# Revit family: PURY-EM200YNW-A
name_source: partatom
category: Mechanical Equipment
revit_build: Autodesk Revit 2016 (Build: 20150220_1215(x64)
units: mm (PartAtom-declared; Revit-internal decimal feet)

## family parameters
Always vertical = Yes
Cut with Voids When Loaded = No
OmniClass Number = 23.75.00.00
OmniClass Title = Climate Control (HVAC)
Part Type = Normal
Room Calculation Point = No
Round Connector Dimension = Use Radius
Shared = No
Work Plane-Based = No

## types (6) — shared parameters
Airflow Rate (m3/h) = 10200
Airflow Rate (m3/min) = 170
Compressor Motor Output (kW) = 6
Compressor_Lubricant = MEL46EH
Compressor_Quantity = 1
Compressor_Type = Inverter scroll hermetic compressor
Cooling Capacity (kW) = 22.4
Cooling EER (kW/kW) = 3.64
Cooling Power Input (kW) = 6.15
Depth = 740 mm  [stored 2.42782 ft]
External Finish = Pre-coated galvanized steel sheets (+powder coating for -BS type) <MUNSELL 5Y 8/1 or similar>
Fan Motor Output (kW) = 0.92
Fan_Quantity = 1
Fan_Type = Propeller Fan
Heating COP (kW/kW) = 3.69
Heating Capacity (kW) = 25
Heating Power Input (kW) = 6.77
Height = 1858 mm  [stored 6.0958 ft]
High pressure pipe_radius = 8 mm  [stored 0.0262467 ft]
Indoor Unit Model/Quantity = WP10 to WP125/1 to 30
Indoor Unit Total Capacity = 50 to 150% of outdoor unit capacity
Low pressure pipe_radius = 10 mm  [stored 0.0328084 ft]
Manufacturer = Mitsubishi Electric Corporation
Maximum Circuit Ampacity (A) = 16.1
Model = PURY-EM200YNW-A
Note_1 = Refrigerant pipe diameters may change depending on the installation condition. Please refer to the installation manual.
Outdoor unit Breaker size (A) = 30
Phase = 3
Protection Devices_High pressure (MPa) = High pressure sensor, High pressure switch at 4.15
Protection Devices_Inverter circuit (COMP./FAN) = Over-heat protection, Over-current protection
Refrigerant Charge (kg) = 5.2
Refrigerant type = R32
Sound Pressure Level (dB(A)) Cooling mode = 59
Sound Pressure Level (dB(A)) Heating mode = 59
Space View = Yes
Subcategory = HVAC
Temp. range of cooling (Indoor temp.) (W.B.) = 15.0 to 24.0
Temp. range of cooling (Outdoor temp.) (D.B.) = -5.0 to 52.0
Temp. range of heating (Indoor temp.) (D.B.) = 15.0 to 27.0
Temp. range of heating (Outdoor temp.) (W.B.) = -20.0 to 15.5
URL = http://www.mitsubishielectric.com
Unit Weight (kg) = 237
Width = 920 mm  [stored 3.01837 ft]
zero-valued in all types: External static pressure (Pa)

## per-type parameters (varying)
| type | Cooling Current (A) | Heating Current (A) | Hertz | Rated Load Ampacity (A) Cooling mode | Rated Load Ampacity (A) Heating mode | Voltage |
| PURY-EM200YNW-A _380V_50Hz | 10.3 | 11.4 | 50 Hz | 10.3 | 11.4 | 380 V |
| PURY-EM200YNW-A _380V_60Hz | 10.3 | 11.4 | 60 Hz | 10.3 | 11.4 | 380 V |
| PURY-EM200YNW-A _400V_50Hz | 9.8 | 10.8 | 50 Hz | 9.8 | 10.8 | 400 V |
| PURY-EM200YNW-A _400V_60Hz | 9.8 | 10.8 | 60 Hz | 9.8 | 10.8 | 400 V |
| PURY-EM200YNW-A _415V_50Hz | 9.5 | 10.4 | 50 Hz | 9.5 | 10.4 | 415 V |
| PURY-EM200YNW-A _415V_60Hz | 9.5 | 10.4 | 60 Hz | 9.5 | 10.4 | 415 V |

note: [stored X ft] marks values corroborated as IEEE doubles in the binary element streams (Revit-internal decimal feet)

## geometry (parser evidence)
native form markers: Blend x76, Sweep x3
no freeform markers — native parametric forms only
